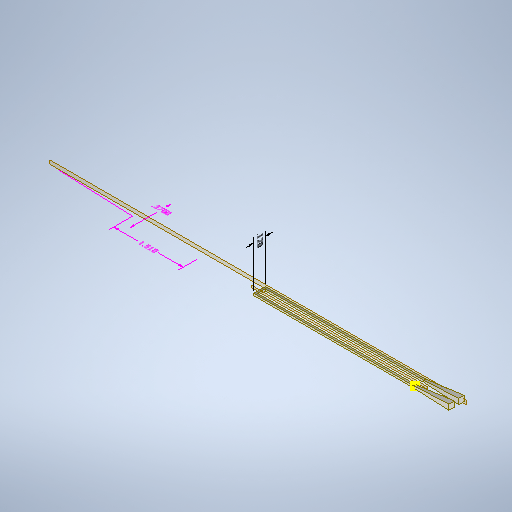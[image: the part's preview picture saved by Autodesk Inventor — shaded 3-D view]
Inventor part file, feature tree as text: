
AUTODESK INVENTOR PART (.ipt)
format: ipt  version: 2025.2 (Build 292293000, 293)  size: 305,152 bytes
history: native  units: in
note: dims shown in document units (in); Inventor stores cm internally (conversion verified against a paired STEP export)
features: other x5, plane x4, sketch x4, sweep x1, loft x1, mirror x1, projected_geometry x1
ambient origin geometry x8: Origin, YZ Plane, XZ Plane, XY Plane, X Axis, Y Axis, Z Axis, Center Point
bodies: Solid1 (feature_tree)
feature tree (17):
  other  "Annotations"
  sweep  "Sweep1"
  plane  "Work Plane1"
  plane  "Work Plane2"
  plane  "Work Plane4"
  sketch  "Sketch15"  dims[d86=-0.1175in]
  sketch  "Sketch16"  dims[d89=0.1in d90=0.0in d91=0.0in d92=0.0in d98=0.02in d99=0.02in d100=0.055in d102=0.055in d104=0.0in d109=0.0in d110=90.0deg d111=0.0in d112=90.0deg d116=-0.06in d113=0.0in d114=0.3937in d115=0.12in d42=0.2341in d43=0.169in d44=0.37in d48=0.2141in d49=0.2512in d50=1.51in]
  loft  "Loft3"
  plane  "Work Plane5"
  mirror  "Mirror3"
  sketch  "Sketch1"  dims[d6=0.0in d7=0.0in d11=0.375in d19=-0.25in]
  sketch  "Sketch2"  dims[d69=1.625in d70=1.625in]
  projected_geometry  "Projected Loop1"
  other  "Edges4"
  other  "Linear Dimension 1"
  other  "Linear Dimension 3"
  other  "Linear Dimension 4"
